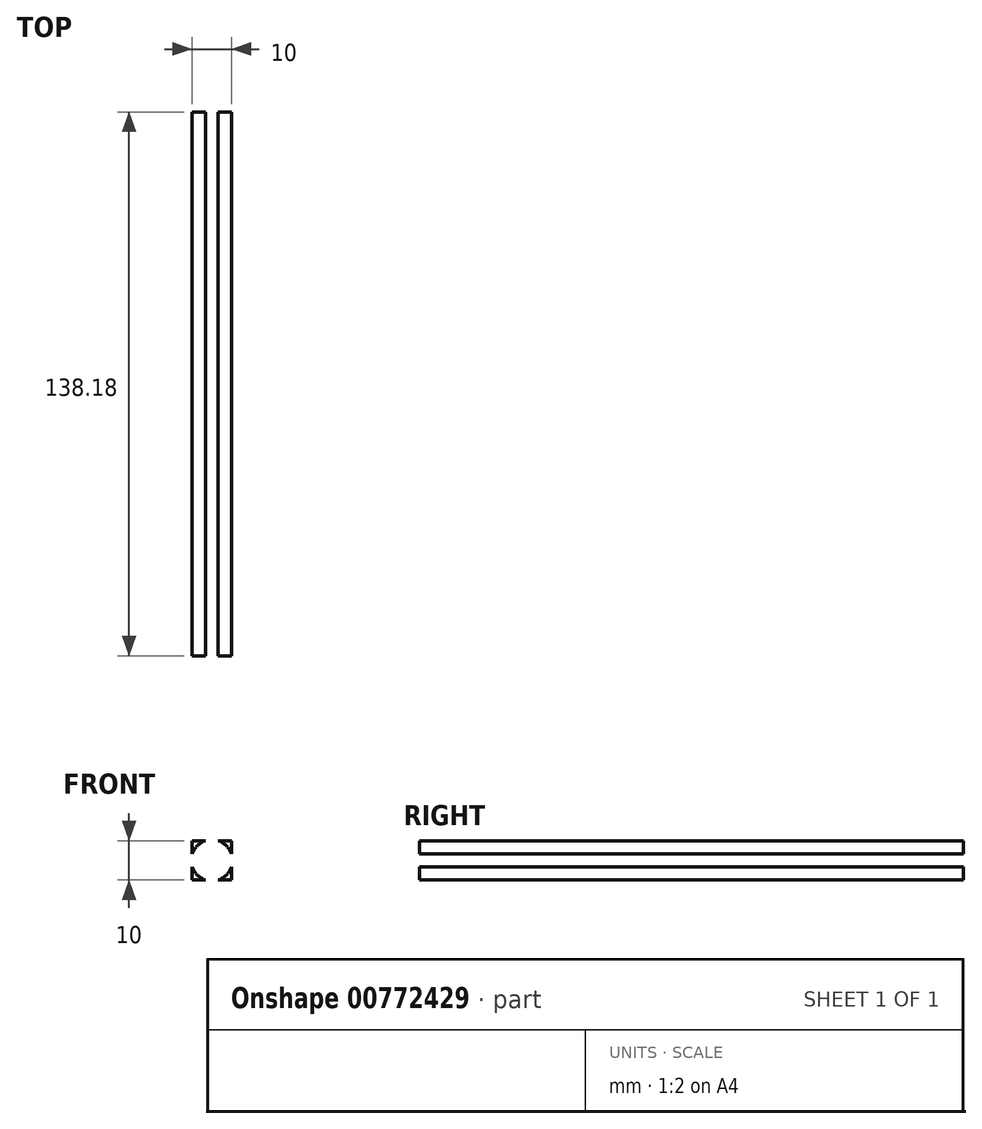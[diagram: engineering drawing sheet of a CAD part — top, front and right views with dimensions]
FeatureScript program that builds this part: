
annotation { "Feature Type Name" : "Feature", "Feature Type Description" : "" }
export const myFeature = defineFeature(function(context is Context, id is Id, definition is map)
    precondition{}
    {
        {
            var Q0;
            Q0=qCreatedBy(makeId("Front.planeOp"),FACE);
            var sketch = newSketch(context, id + "F0", { "sketchPlane" : qUnion([Q0])});
            skLineSegment(sketch, "E0.bottom", {"start": v(-30.8, 26.57) * mm, "end": v(-20.8, 26.57) * mm});
            skLineSegment(sketch, "E0.top", {"start": v(-30.8, 16.57) * mm, "end": v(-20.8, 16.57) * mm});
            skLineSegment(sketch, "E0.left", {"start": v(-30.8, 26.57) * mm, "end": v(-30.8, 16.57) * mm});
            skLineSegment(sketch, "E0.right", {"start": v(-20.8, 26.57) * mm, "end": v(-20.8, 16.57) * mm});
            skSolve(sketch);
        }
        {
            var Q0;
            Q0=makeQuery(id+"F0.imprint","IMPRINT",FACE,{"disambiguationData":[TD([[makeQuery(id+"F0.imprint","IMPRINT",EDGE,{"derivedFrom":sQuery(id+"F0.wireOp",EDGE,"E0.bottom")}),-1.0]])]});
            extrude(context, id + "F1", {"entities" : qUnion([Q0]), "depth" : 138.18 * mm, "offsetDistance" : 25 * mm});
        }
        {
            var Q0;
            Q0=makeQuery(id+"F1.opExtrude","CAP_FACE",FACE,{"disambiguationData":[OSD([sQuery(id+"F0.wireOp",EDGE,"E0.bottom"),sQuery(id+"F0.wireOp",EDGE,"E0.top"),sQuery(id+"F0.wireOp",EDGE,"E0.left"),sQuery(id+"F0.wireOp",EDGE,"E0.right")])],"isStart":false});
            var sketch = newSketch(context, id + "F2", { "sketchPlane" : qUnion([Q0])});
            skCircle(sketch, "E1", {"center": v(-25.8, 21.57) * mm, "radius": 5.25 * mm});
            skPoint(sketch, "E1.centerSnap0", {"position": v(-30.8, 21.57) * mm});
            skPoint(sketch, "E1.centerSnap1", {"position": v(-25.8, 26.57) * mm});
            skSolve(sketch);
        }
        {
            var Q0;
            {var subQ0=sQuery(id+"F2.wireOp",EDGE,"E1");var subQ1=makeQuery(id+"F2.imprint","INTERSECT",VERTEX,{"derivedFrom":[makeQuery(id+"F1.opExtrude","CAP_EDGE",EDGE,{"disambiguationData":[OSD([sQuery(id+"F0.wireOp",EDGE,"E0.bottom")])],"isStart":false}),subQ0]});Q0=makeQuery(id+"F2.imprint","IMPRINT",FACE,{"disambiguationData":[TD([[makeQuery(id+"F2.imprint","IMPRINT",EDGE,{"disambiguationData":[TD([[subQ1,1.0]])],"derivedFrom":subQ0}),1.0]])]});}
            extrude(context, id + "F3", {"entities" : qUnion([Q0]), "operationType" : NewBodyOperationType.REMOVE, "endBound" : BoundingType.THROUGH_ALL, "oppositeDirection" : true, "depth" : 25 * mm, "offsetDistance" : 25 * mm});
        }
        {
            var Q0;
            {var subQ0=sQuery(id+"F2.wireOp",EDGE,"E1");var subQ8=makeQuery(id+"F1.opExtrude","CAP_EDGE",EDGE,{"disambiguationData":[OSD([sQuery(id+"F0.wireOp",EDGE,"E0.bottom")])],"isStart":false});var subQ11=makeQuery(id+"F2.imprint","INTERSECT",VERTEX,{"disambiguationData":[OD(0.0)],"derivedFrom":[subQ8,subQ0]});Q0=makeQuery(id+"F2.imprint","IMPRINT",FACE,{"disambiguationData":[TD([[makeQuery(id+"F2.imprint","IMPRINT",EDGE,{"disambiguationData":[TD([[subQ11,1.0]])],"derivedFrom":subQ0}),1.0]])]});}
            extrude(context, id + "F4", {"entities" : qUnion([Q0]), "operationType" : NewBodyOperationType.REMOVE, "endBound" : BoundingType.THROUGH_ALL, "oppositeDirection" : true, "depth" : 25 * mm, "offsetDistance" : 25 * mm});
        }
    });
